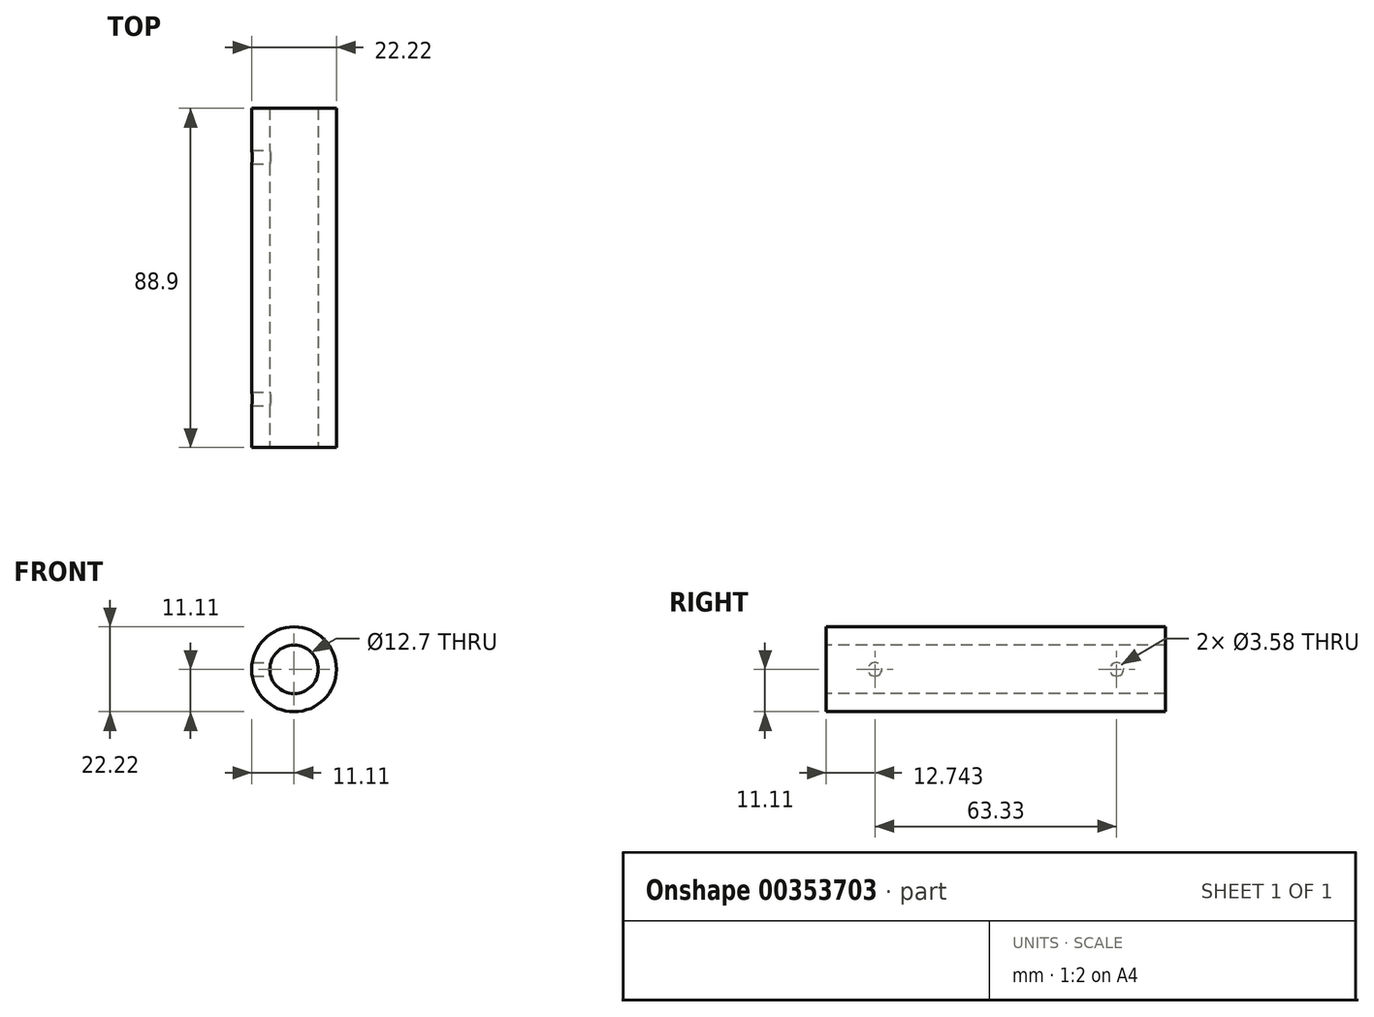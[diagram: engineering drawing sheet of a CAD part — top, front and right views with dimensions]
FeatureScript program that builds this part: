
annotation { "Feature Type Name" : "Feature", "Feature Type Description" : "" }
export const myFeature = defineFeature(function(context is Context, id is Id, definition is map)
    precondition{}
    {
        {
            var Q0;
            Q0=qCreatedBy(makeId("Front.planeOp"),FACE);
            var sketch = newSketch(context, id + "F0", { "sketchPlane" : qUnion([Q0])});
            skCircle(sketch, "E0", {"center": v(0, 0) * mm, "radius": 11.11 * mm});
            skSolve(sketch);
        }
        {
            var Q0;
            Q0 = qSketchRegion(id + "F0", true);
            extrude(context, id + "F1", {"entities" : qUnion([Q0]), "depth" : 88.9 * mm, "symmetric" : true});
        }
        {
            var Q0;
            Q0=makeQuery(id+"F1.opExtrude","CAP_FACE",FACE,{"disambiguationData":[OSD([sQuery(id+"F0.wireOp",EDGE,"E0")])],"isStart":false});
            var sketch = newSketch(context, id + "F2", { "sketchPlane" : qUnion([Q0])});
            skCircle(sketch, "E1", {"center": v(0, 0) * mm, "radius": 6.35 * mm});
            skSolve(sketch);
        }
        {
            var Q0;
            Q0 = qSketchRegion(id + "F2", true);
            extrude(context, id + "F3", {"entities" : qUnion([Q0]), "operationType" : NewBodyOperationType.REMOVE, "oppositeDirection" : true, "depth" : 88.9 * mm});
        }
        {
            var Q0;
            Q0=qCreatedBy(makeId("Right.planeOp"),FACE);
            var sketch = newSketch(context, id + "F4", { "sketchPlane" : qUnion([Q0])});
            skLineSegment(sketch, "E2", {"start": v(44.27, 0) * mm, "end": v(31.62, 0) * mm, "construction": true});
            skCircle(sketch, "E3", {"center": v(31.62, 0) * mm, "radius": 1.8 * mm});
            skSolve(sketch);
        }
        {
            var Q0;
            Q0 = qSketchRegion(id + "F4", true);
            extrude(context, id + "F5", {"entities" : qUnion([Q0]), "operationType" : NewBodyOperationType.REMOVE, "oppositeDirection" : true, "depth" : 25.4 * mm});
        }
        {
            var Q0;
            Q0=qCreatedBy(makeId("Right.planeOp"),FACE);
            var sketch = newSketch(context, id + "F6", { "sketchPlane" : qUnion([Q0])});
            skLineSegment(sketch, "E4", {"start": v(-44.4, 0) * mm, "end": v(-31.7, 0) * mm, "construction": true});
            skCircle(sketch, "E5", {"center": v(-31.7, 0) * mm, "radius": 1.8 * mm});
            skSolve(sketch);
        }
        {
            var Q0;
            Q0 = qSketchRegion(id + "F6", true);
            extrude(context, id + "F7", {"entities" : qUnion([Q0]), "operationType" : NewBodyOperationType.REMOVE, "oppositeDirection" : true, "depth" : 25.4 * mm});
        }
    });
